# Revit family: agtatec_Record_SldngDrset_E-STA_Standalone
name_source: partatom
category: Doors
revit_build: Autodesk Revit Architecture 2015 (Build: 20140606_1530(x64)
units: mm (PartAtom-declared; Revit-internal decimal feet)

## types (12) — shared parameters
AccessoryOptions = Contact manufacturer
AcousticRating = None
AlternativeDoorsetGlazing = Part of glazing spec
AntiFingerTrapRequirement = Yes
Assembly Code = B2030110
BIMObjectName = agtatec_Record_SlidingDoorset_E-STA_Standalone
CladdingProfile = Yes
ClearHeightOfPassage = 2187 mm  [stored 7.1752 ft]
ClearanceZones = No
Colour = Customer specific
Configuration = 1 or 2
Construction Type = Automatic Sliding Door
Description = Automatic Sliding Door
DistanceToWall = 57 mm  [stored 0.187008 ft]
DoorIncluded = Yes
DoorOpeningLeft = 1300 mm  [stored 4.26509 ft]
DoorOpeningRight = 1300 mm  [stored 4.26509 ft]
DoorSeal = yes
DoorsetFasteners = Screws
DoorsetOperation = Automatic
DriveDepth = 194 mm  [stored 0.636483 ft]
DriveDepth2 = 37 mm  [stored 0.121391 ft]
DriveUnit = agtatec_Record_Sliding Door, Sheet Metal (Painted Steel)
DurationUnit = year
ElectronicLock = Yes
Finish = Powder coated, Anodized, customer specific
FireExit = No
FireRating = None
FloorGuide = agtatec_Record_Sliding Door, Stainless Steel
FrameMaterial = Aluminium
FrameProfile = Aluminium
FrameSeal = Yes
Function = Exterior
GlassLayers = 2
GlassThickness1 = 6 mm (default)
GlassThickness2 = 6 mm (default)
GlassType = Part of glazing spec
GlazingAreaFraction = Depends on size. Can be calculated
HandicapAccessible = Yes
HasDrive = Yes
IfcExportAs = ifcDoorStyle
IfcExportType = Door
InnerPanelWidth = 1232 mm  [stored 4.04199 ft]
InterlancingProfileHeight = 2195 mm  [stored 7.20144 ft]
IsExternal = Yes
LeafColourOptions = All RAL, customer specific
ManufacturerName = Record
ManufacturerURL = www.agta-record.com
Material = Aluminium
Model = record Standard Linear Slider
ModelReference = Depends on the configuration
NBSDescription = Sliding Doorset
NBSReference = 25-50-20/175
Name = SldngDrset_E-STA_Standalone_Record
OpeningWidth = 1200 mm
OuterPanelWidthLeft = 1273 mm  [stored 4.17651 ft]
OuterPanelWidthRight = 1273 mm  [stored 4.17651 ft]
PanelFill = agtatec_Record_Sliding Door, Laminated Safety Glass (Clear)
PanelFrames = agtatec_Record_Sliding Door, Aluminium
PanelHeight = 2200 mm  [stored 7.21785 ft]
PassageMountingLeft = No
PassageMountingProfile(OnlyApplicableForTypesWithTwoSidePanels) = No
PassageMountingRight = No
ProductInformation = www.agta-record.com
ReferenceStandard = EN16005, EN16361, DIN 18650, etc.
ReplacementCost = Depends on the configuration and door type
SecurityRating = None
SelfClosing = Yes
ServiceLifeDuration = 10-15 years
Shape = Rectangular
SidePanelMinimumStandard = 1282 mm  [stored 4.20604 ft]
SidePanelWidthLeft = 1300 mm  [stored 4.26509 ft]
SidePanelWidthRight = 1300 mm  [stored 4.26509 ft]
SmokeStop = No
SupportLength = 2493 mm  [stored 8.17913 ft]
ThresholdRequired = Yes
ThresholdStripping = No additional required, part of the doorset
URL = www.agta-record.com
Uniclass2 = Ss_25_30_20_77
Version = Version 1.0
WallMountingProfile = Yes
WarrantyDescription = Depends on country
WarrantyDurationLabour = Depends on country
WarrantyDurationParts = Depends on country
WarrantyDurationUnit = Depends on country
WarrantyGuarantorLabour = Local door manufacturer
WarrantyGuarantorParts = Local door manufacturer
Weight = Depends on configuration and size
WithDriveCladding = Yes
WithinStandardSizes = Yes
WithoutDriveCladding(OnlyApplicableForTypesWithoutSidePanels) = No
zero-valued in all types: Cost, DoorOpening, DoorOpeningRestriction, DriveUnitExtraWidthLeft, DriveUnitExtraWidthRight, ExtraLeft, ExtraRight, ExtraWidthLeft, ExtraWidthRight, NominalLength, ProfileOpeningLeft, ProfileOpeningRight, ThermalTransmittance

## per-type parameters (varying)
| type | CenterOfDoor | CladdingVoid | ClearanceZoneLeft | ClearanceZoneRight | DriveUnitHeight | Height | InterlancingProfileLeft | InterlancingProfileRight | LeftPanel | NominalHeight | NominalWidth | RightPanel | Rough Height | Rough Width | SupportLengthLeft | SupportLengthRight | TotalHeight | TotalWidth | WallMountingLeft | WallMountingRight | WallOpeningWidth | Width | WithoutSidePanels |
| E-STA-L 150 mm drive unit height - left - with side panel | 2514.5 mm  [stored 8.24967 ft] | 41 mm  [stored 0.134514 ft] | 1269.5 mm  [stored 4.16503 ft] | 1301.5 mm  [stored 4.27001 ft] | 150 mm | 2337 mm  [stored 7.66732 ft] | Yes | No | Yes | 2337 mm  [stored 7.66732 ft] | 2555 mm  [stored 8.38255 ft] | No | 2343 mm  [stored 7.68701 ft] | 2561 mm | 1877 mm | 616 mm  [stored 2.021 ft] | 2337 mm  [stored 7.66732 ft] | 2555 mm  [stored 8.38255 ft] | Yes | No | 2500 mm  [stored 8.2021 ft] | 2555 mm  [stored 8.38255 ft] | No |
| E-STA-R 150 mm drive unit height - right - without side panel | 1253.5 mm  [stored 4.11253 ft] | 9 mm  [stored 0.0295276 ft] | 1301.5 mm  [stored 4.27001 ft] | 1246.5 mm  [stored 4.08957 ft] | 150 mm | 2337 mm  [stored 7.66732 ft] | No | Yes | No | 2337 mm  [stored 7.66732 ft] | 1310 mm  [stored 4.2979 ft] | No | 2343 mm  [stored 7.68701 ft] | 1316 mm  [stored 4.31759 ft] | 616 mm  [stored 2.021 ft] | 1877 mm | 2337 mm  [stored 7.66732 ft] | 1310 mm  [stored 4.2979 ft] | No | No | 1200 mm | 1310 mm  [stored 4.2979 ft] | Yes |
| E-STA-R 150 mm drive unit height - right - with side panel | 1253.5 mm  [stored 4.11253 ft] | 41 mm  [stored 0.134514 ft] | 1301.5 mm  [stored 4.27001 ft] | 1269.5 mm  [stored 4.16503 ft] | 150 mm | 2337 mm  [stored 7.66732 ft] | No | Yes | No | 2337 mm  [stored 7.66732 ft] | 2555 mm  [stored 8.38255 ft] | Yes | 2343 mm  [stored 7.68701 ft] | 2561 mm | 616 mm  [stored 2.021 ft] | 1877 mm | 2337 mm  [stored 7.66732 ft] | 2555 mm  [stored 8.38255 ft] | No | Yes | 2500 mm  [stored 8.2021 ft] | 2555 mm  [stored 8.38255 ft] | No |
| E-STA-L 150 mm drive unit height - left - without side panel | 2514.5 mm  [stored 8.24967 ft] | 9 mm  [stored 0.0295276 ft] | 1246.5 mm  [stored 4.08957 ft] | 1301.5 mm  [stored 4.27001 ft] | 150 mm | 2337 mm  [stored 7.66732 ft] | Yes | No | No | 2337 mm  [stored 7.66732 ft] | 1310 mm  [stored 4.2979 ft] | No | 2343 mm  [stored 7.68701 ft] | 1316 mm  [stored 4.31759 ft] | 1877 mm | 616 mm  [stored 2.021 ft] | 2337 mm  [stored 7.66732 ft] | 1310 mm  [stored 4.2979 ft] | No | No | 1200 mm | 1310 mm  [stored 4.2979 ft] | Yes |
| E-STA-L 200 mm drive unit height - left - with side panel | 2514.5 mm  [stored 8.24967 ft] | 41 mm  [stored 0.134514 ft] | 1269.5 mm  [stored 4.16503 ft] | 1301.5 mm  [stored 4.27001 ft] | 200 mm  [stored 0.656168 ft] | 2387 mm  [stored 7.83136 ft] | Yes | No | Yes | 2387 mm  [stored 7.83136 ft] | 2555 mm  [stored 8.38255 ft] | No | 2393 mm  [stored 7.85105 ft] | 2561 mm | 1877 mm | 616 mm  [stored 2.021 ft] | 2387 mm  [stored 7.83136 ft] | 2555 mm  [stored 8.38255 ft] | Yes | No | 2500 mm  [stored 8.2021 ft] | 2555 mm  [stored 8.38255 ft] | No |
| E-STA-L 200 mm drive unit height - left - without side panel | 2514.5 mm  [stored 8.24967 ft] | 9 mm  [stored 0.0295276 ft] | 1246.5 mm  [stored 4.08957 ft] | 1301.5 mm  [stored 4.27001 ft] | 200 mm  [stored 0.656168 ft] | 2387 mm  [stored 7.83136 ft] | Yes | No | No | 2387 mm  [stored 7.83136 ft] | 1310 mm  [stored 4.2979 ft] | No | 2393 mm  [stored 7.85105 ft] | 1316 mm  [stored 4.31759 ft] | 1877 mm | 616 mm  [stored 2.021 ft] | 2387 mm  [stored 7.83136 ft] | 1310 mm  [stored 4.2979 ft] | No | No | 1200 mm | 1310 mm  [stored 4.2979 ft] | Yes |
| E-STA-R 200 mm drive unit height - right - with side panel | 1253.5 mm  [stored 4.11253 ft] | 41 mm  [stored 0.134514 ft] | 1301.5 mm  [stored 4.27001 ft] | 1269.5 mm  [stored 4.16503 ft] | 200 mm  [stored 0.656168 ft] | 2387 mm  [stored 7.83136 ft] | No | Yes | No | 2387 mm  [stored 7.83136 ft] | 2555 mm  [stored 8.38255 ft] | Yes | 2393 mm  [stored 7.85105 ft] | 2561 mm | 616 mm  [stored 2.021 ft] | 1877 mm | 2387 mm  [stored 7.83136 ft] | 2555 mm  [stored 8.38255 ft] | No | Yes | 2500 mm  [stored 8.2021 ft] | 2555 mm  [stored 8.38255 ft] | No |
| E-STA-R 200 mm drive unit height - right - without side panel | 1253.5 mm  [stored 4.11253 ft] | 9 mm  [stored 0.0295276 ft] | 1301.5 mm  [stored 4.27001 ft] | 1246.5 mm  [stored 4.08957 ft] | 200 mm  [stored 0.656168 ft] | 2387 mm  [stored 7.83136 ft] | No | Yes | No | 2387 mm  [stored 7.83136 ft] | 1310 mm  [stored 4.2979 ft] | No | 2393 mm  [stored 7.85105 ft] | 1316 mm  [stored 4.31759 ft] | 616 mm  [stored 2.021 ft] | 1877 mm | 2387 mm  [stored 7.83136 ft] | 1310 mm  [stored 4.2979 ft] | No | No | 1200 mm | 1310 mm  [stored 4.2979 ft] | Yes |
| E-STA-L 108 mm drive unit height - left - with side panel | 2514.5 mm  [stored 8.24967 ft] | 41 mm  [stored 0.134514 ft] | 1269.5 mm  [stored 4.16503 ft] | 1301.5 mm  [stored 4.27001 ft] | 108 mm  [stored 0.354331 ft] | 2295 mm | Yes | No | Yes | 2295 mm | 2555 mm  [stored 8.38255 ft] | No | 2301 mm | 2561 mm | 1877 mm | 616 mm  [stored 2.021 ft] | 2295 mm | 2555 mm  [stored 8.38255 ft] | Yes | No | 2500 mm  [stored 8.2021 ft] | 2555 mm  [stored 8.38255 ft] | No |
| E-STA-L 108 mm drive unit height - left - without side panel | 2514.5 mm  [stored 8.24967 ft] | 9 mm  [stored 0.0295276 ft] | 1246.5 mm  [stored 4.08957 ft] | 1301.5 mm  [stored 4.27001 ft] | 108 mm  [stored 0.354331 ft] | 2295 mm | Yes | No | No | 2295 mm | 1310 mm  [stored 4.2979 ft] | No | 2301 mm | 1316 mm  [stored 4.31759 ft] | 1877 mm | 616 mm  [stored 2.021 ft] | 2295 mm | 1310 mm  [stored 4.2979 ft] | No | No | 1200 mm | 1310 mm  [stored 4.2979 ft] | Yes |
| E-STA-R 108 mm drive unit height - right - with side panel | 1253.5 mm  [stored 4.11253 ft] | 41 mm  [stored 0.134514 ft] | 1301.5 mm  [stored 4.27001 ft] | 1269.5 mm  [stored 4.16503 ft] | 108 mm  [stored 0.354331 ft] | 2295 mm | No | Yes | No | 2295 mm | 2555 mm  [stored 8.38255 ft] | Yes | 2301 mm | 2561 mm | 616 mm  [stored 2.021 ft] | 1877 mm | 2295 mm | 2555 mm  [stored 8.38255 ft] | No | Yes | 2500 mm  [stored 8.2021 ft] | 2555 mm  [stored 8.38255 ft] | No |
| E-STA-R 108 mm drive unit height - right - without side panel | 1253.5 mm  [stored 4.11253 ft] | 9 mm  [stored 0.0295276 ft] | 1301.5 mm  [stored 4.27001 ft] | 1246.5 mm  [stored 4.08957 ft] | 108 mm  [stored 0.354331 ft] | 2295 mm | No | Yes | No | 2295 mm | 1310 mm  [stored 4.2979 ft] | No | 2301 mm | 1316 mm  [stored 4.31759 ft] | 616 mm  [stored 2.021 ft] | 1877 mm | 2295 mm | 1310 mm  [stored 4.2979 ft] | No | No | 1200 mm | 1310 mm  [stored 4.2979 ft] | Yes |

note: [stored X ft] marks values corroborated as IEEE doubles in the binary element streams (Revit-internal decimal feet)

## geometry (parser evidence)
native form markers: Sweep x11
no freeform markers — native parametric forms only
